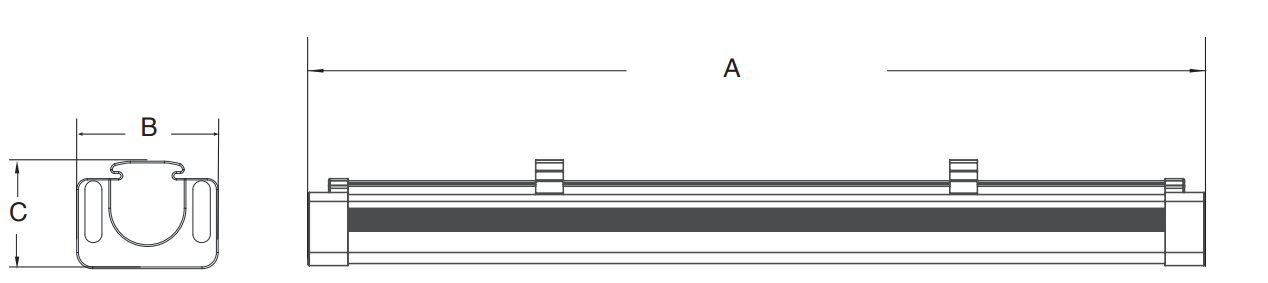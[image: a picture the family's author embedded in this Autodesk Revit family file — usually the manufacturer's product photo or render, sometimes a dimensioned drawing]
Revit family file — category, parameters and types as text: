
# Revit family: SPALED2-4HTHOWT40120-277V
name_source: partatom
category: Lighting Fixtures
revit_build: Autodesk Revit LT 2015 (Build: 20140606_1530(x64)
units: mm (PartAtom-declared; Revit-internal decimal feet)

## types (2) — shared parameters
Color Filter = 16777215
Default Elevation = 4' - 0"
Description = The vandal resistant design of the SPADA® makes it ideal for
manufacturing facilities, work stations, locker rooms, schools,
breezeways, government facilities, prisons and public areas.
Dimming Lamp Color Temperature Shift = <None>
Emit from Line Length = 2' - 0"
L = 1' - 0"
LENGTH = 2' - 0"
Lamp = LED
Manufacturer = BEGHELLI
Model = SPADA
Photometric Web File = SPA-2-HT-40W-WT40-120-277V-MOD.ies
Tilt Angle = -90.00°
Type Comments = SPADA® is DesignLights Consortium® qualified
for Direct Linear Ambient Luminaires.
Type Image = SPADA PICTURE.PNG

## per-type parameters (varying)
| type | Wattage Comments |
| SPALED2HTLOWT40120-277V | 18.6W |
| SPALED4HTHOWT40120-277V | 38.2W |

## geometry (parser evidence)
native form markers: Sweep x9
no freeform markers — native parametric forms only
